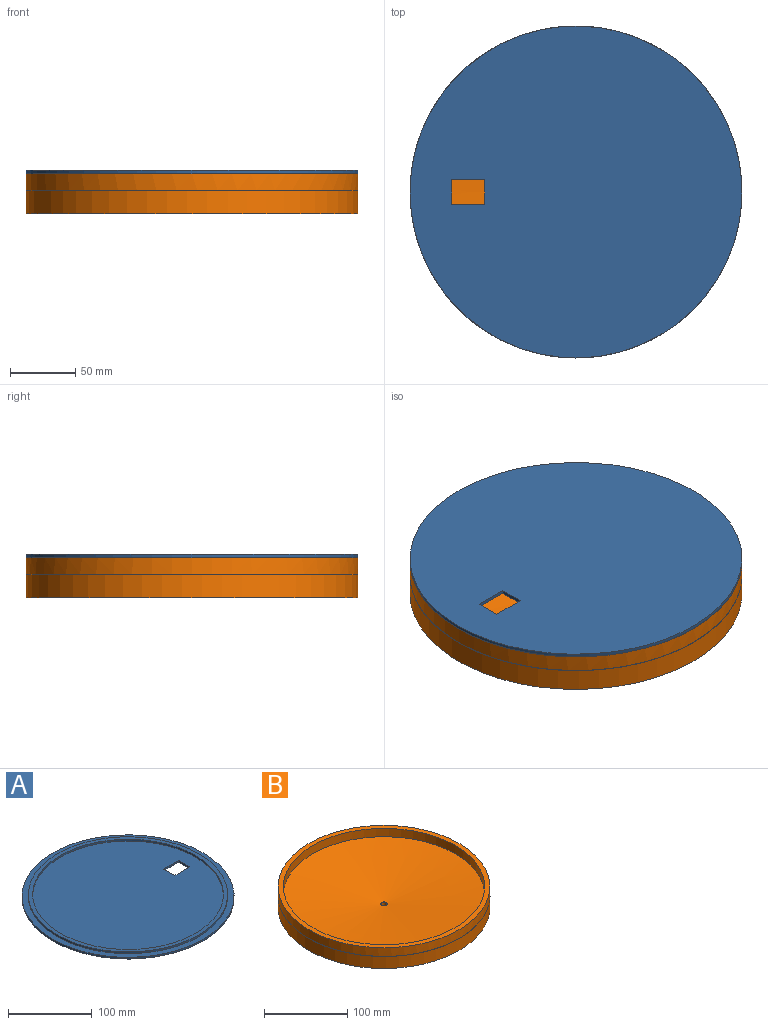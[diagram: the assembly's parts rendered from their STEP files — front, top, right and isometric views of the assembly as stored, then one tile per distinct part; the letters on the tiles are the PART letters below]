
ASSEMBLY  parts=2 mates=1
PART A: 11 faces, bbox 254x254x5.1 mm
  f0: plane 254x254mm, normal (0,0,-1), area 50186.9mm2, adj f2,f7,f8,f9,f10
  f1: plane 228.6x228.6mm, normal (0,0,1), area 40559.4mm2, adj f4,f7,f8,f9,f10
  f2: cylinder r=127mm len=254mm, axis (0,0,-1), area 2026.8mm2, adj f0,f3
  f3: plane 254x254mm, normal (0,0,1), area 5898.1mm2, adj f2,f5
  f4: cylinder r=114.3mm len=228.6mm, axis (0,0,-1), area 1824.1mm2, adj f1,f6
  f5: cylinder r=119.38mm len=238.76mm, axis (0,0,-1), area 1905.2mm2, adj f3,f6
  f6: plane 238.76x238.76mm, normal (0,0,1), area 3729.4mm2, adj f4,f5
  f7: plane 19.05x2.54mm, normal (-1,0,0), area 48.4mm2, adj f0,f1,f8,f10
  f8: plane 25.4x2.54mm, normal (0,1,0), area 64.5mm2, adj f0,f1,f7,f9
  f9: plane 19.05x2.54mm, normal (1,0,0), area 48.4mm2, adj f0,f1,f8,f10
  f10: plane 25.4x2.54mm, normal (0,-1,0), area 64.5mm2, adj f0,f1,f7,f9
PART B: 13 faces, bbox 254x254x30.5 mm
  f0: plane 7.93x7.93mm, normal (0,0,1), area 12.5mm2, adj f3,f4
  f1: cylinder r=127mm len=254mm, axis (0,0,-1), area 14073.4mm2, adj f2,f9
  f2: plane 254x254mm, normal (0,0,-1), area 50633.8mm2, adj f1,f3
  f3: cylinder r=3.43mm len=6.86mm, axis (0,0,1), area 109.4mm2, adj f0,f2
  f4: cone r=3.97mm half-angle=83.5deg, axis (0,0,1), area 45975mm2, adj f0,f7
  f5: cylinder r=127mm len=254mm, axis (0,0,-1), area 10186.9mm2, adj f6,f8
  f6: plane 254x254mm, normal (0,0,1), area 4940.4mm2, adj f5,f7
  f7: cylinder r=120.65mm len=241.3mm, axis (0,0,-1), area 9200.9mm2, adj f4,f6
  f8: cone r=126.87mm half-angle=5.4deg, axis (0,0,-1), area 61.3mm2, adj f5,f9
  f9: cone r=16.53mm half-angle=83.5deg, axis (0,0,1), area 5.8mm2, adj f1,f8
  f10: cone r=16.53mm half-angle=83.5deg, axis (0,0,1), area 45161mm2, adj f11,f12
  f11: plane 241.3x241.3mm, normal (0,0,1), area 44872mm2, adj f10,f12
  f12: cylinder r=120.65mm len=241.3mm, axis (0,0,-1), area 8971.6mm2, adj f10,f11
PLACE A rot(axis=(0,1,0),180deg) t=(-10.62,1.24,47.24)mm
PLACE B t=(-10.62,1.24,14.22)mm
MATE fastened A.f2 <-> B.f1  axis (0,0,-1) through (-10.62,1.24,44.7)mm
